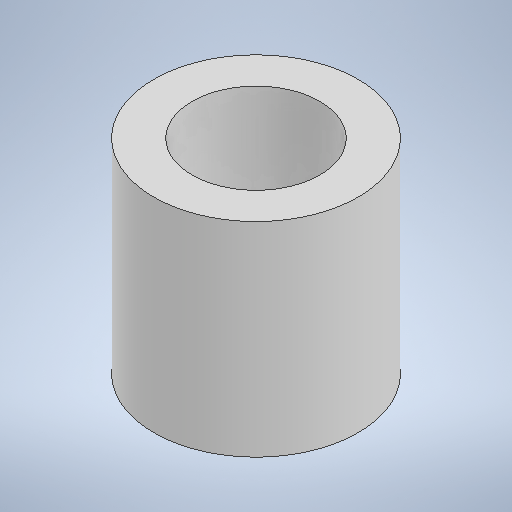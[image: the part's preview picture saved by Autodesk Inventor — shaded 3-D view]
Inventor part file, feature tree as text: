
AUTODESK INVENTOR PART (.ipt)
format: ipt  version: 2025.1 (Build 291241000, 241)  size: 210,432 bytes
history: native  units: mm
features: extrude x1, sketch x1
ambient origin geometry x8: Origin, YZ Plane, XZ Plane, XY Plane, X Axis, Y Axis, Z Axis, Center Point
bodies: Solid1 (feature_tree)
feature tree (2):
  extrude  "Extrusion1"  Depth=8.0mm
  sketch  "Sketch1"  dims[d0=8.0mm d1=5.0mm d2=8.0mm d3=0.0mm]
